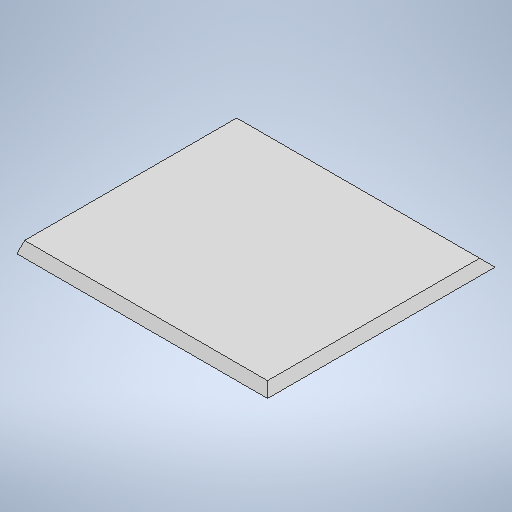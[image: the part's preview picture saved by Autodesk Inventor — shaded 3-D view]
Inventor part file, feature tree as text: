
AUTODESK INVENTOR PART (.ipt)
format: ipt  version: 2025 (Build 290162000, 162)  size: 217,600 bytes
history: native  units: in
note: dims shown in document units (in); Inventor stores cm internally (conversion verified against a paired STEP export)
features: extrude x1, chamfer x1, sketch x1
ambient origin geometry x8: Origin, YZ Plane, XZ Plane, XY Plane, X Axis, Y Axis, Z Axis, Center Point
bodies: Solid1 (feature_tree)
feature tree (3):
  extrude  "Extrusion1"  Depth=0.7874in
  chamfer  "Chamfer3"  Distance=0.7874in
  sketch  "Sketch1"  dims[d0=25.5906in d1=23.2283in d2=0.7874in d3=0.0in d10=0.7874in d11=0.0492in d12=45.0deg]
